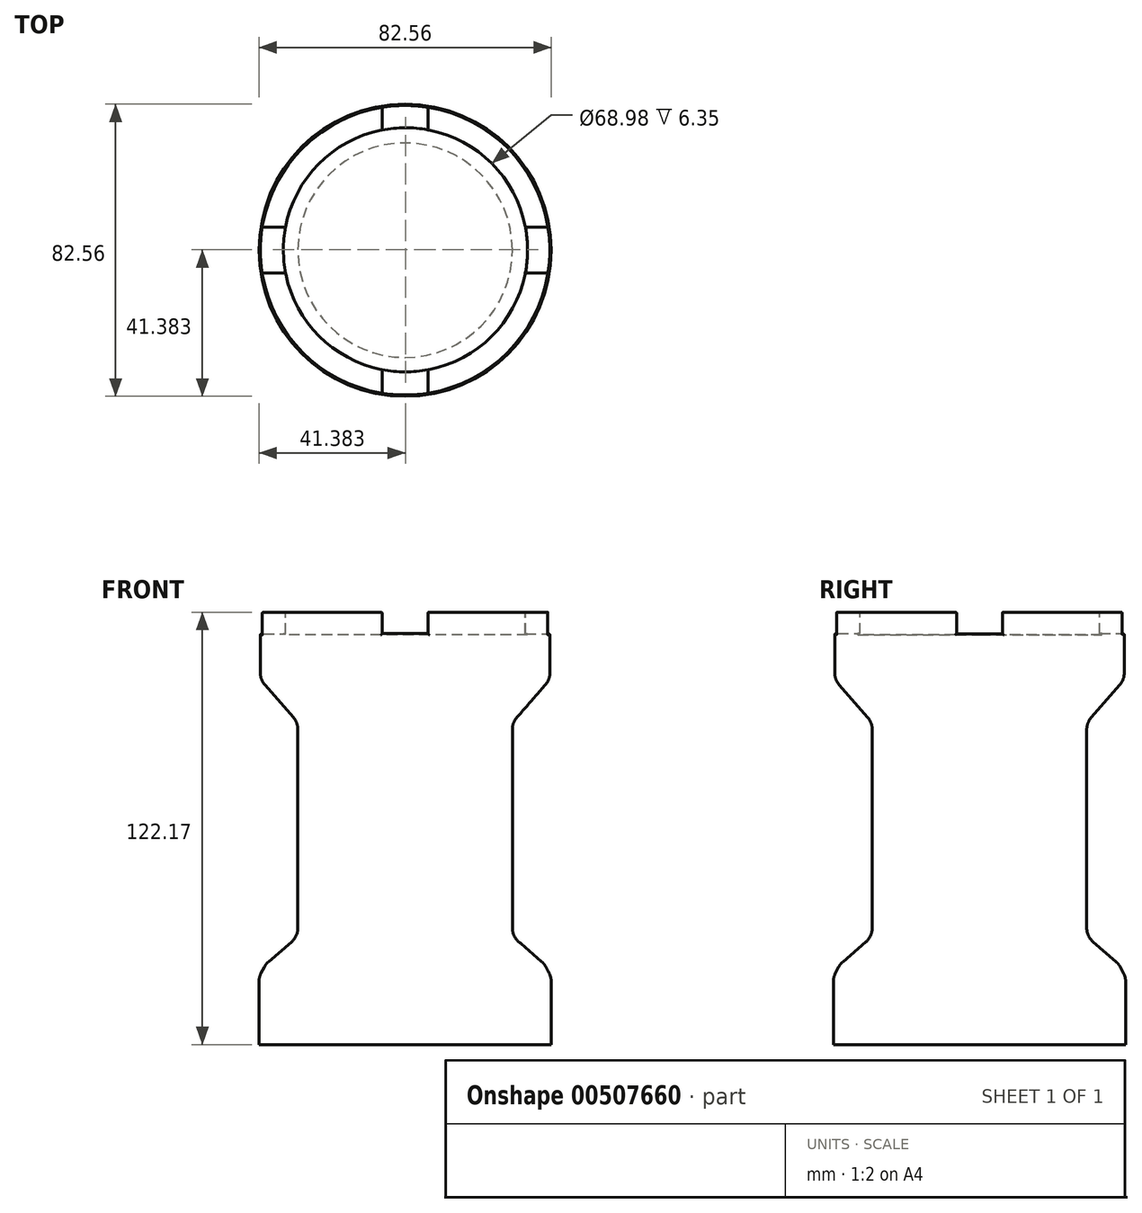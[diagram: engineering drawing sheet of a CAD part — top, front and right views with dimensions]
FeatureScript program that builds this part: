
annotation { "Feature Type Name" : "Feature", "Feature Type Description" : "" }
export const myFeature = defineFeature(function(context is Context, id is Id, definition is map)
    precondition{}
    {
        {
            var Q0;
            Q0=qCreatedBy(makeId("Top.planeOp"),FACE);
            var sketch = newSketch(context, id + "F0", { "sketchPlane" : qUnion([Q0])});
            skCircle(sketch, "E0", {"center": v(0, 0) * mm, "radius": 41.28 * mm});
            skSolve(sketch);
        }
        {
            var Q0;
            Q0=makeQuery(id+"F0.imprint","IMPRINT",FACE,{"disambiguationData":[TD([[makeQuery(id+"F0.imprint","IMPRINT",EDGE,{"derivedFrom":sQuery(id+"F0.wireOp",EDGE,"E0")}),1.0]])]});
            extrude(context, id + "F1", {"entities" : qUnion([Q0]), "depth" : 19.05 * mm, "offsetDistance" : 25.4 * mm});
        }
        {
            var Q0;
            Q0=makeQuery(id+"F1.opExtrude","CAP_FACE",FACE,{"disambiguationData":[OSD([sQuery(id+"F0.wireOp",EDGE,"E0")])],"isStart":false});
            extrude(context, id + "F2", {"entities" : qUnion([Q0]), "operationType" : NewBodyOperationType.ADD, "depth" : 3.68 * mm, "offsetDistance" : 25.4 * mm, "hasDraft" : true, "draftAngle" : 27.5 * degree, "draftPullDirection" : true});
        }
        {
            var Q0;
            Q0=makeQuery(id+"F2.opExtrude","CAP_FACE",FACE,{"disambiguationData":[OSD([sQuery(id+"F0.wireOp",EDGE,"E0")])],"isStart":false});
            extrude(context, id + "F3", {"entities" : qUnion([Q0]), "operationType" : NewBodyOperationType.ADD, "depth" : 7.87 * mm, "offsetDistance" : 25.4 * mm, "hasDraft" : true, "draftAngle" : 49 * degree, "draftPullDirection" : true});
        }
        {
            var Q0;
            Q0=makeQuery(id+"F3.opExtrude","CAP_FACE",FACE,{"disambiguationData":[OSD([sQuery(id+"F0.wireOp",EDGE,"E0")])],"isStart":false});
            extrude(context, id + "F4", {"entities" : qUnion([Q0]), "operationType" : NewBodyOperationType.ADD, "depth" : 60.32 * mm, "offsetDistance" : 25.4 * mm});
        }
        {
            var Q0;
            Q0=makeQuery(id+"F4.opExtrude","CAP_FACE",FACE,{"disambiguationData":[OSD([sQuery(id+"F0.wireOp",EDGE,"E0")])],"isStart":false});
            extrude(context, id + "F5", {"entities" : qUnion([Q0]), "operationType" : NewBodyOperationType.ADD, "depth" : 12.2 * mm, "offsetDistance" : 25.4 * mm, "hasDraft" : true, "draftAngle" : 41 * degree});
        }
        {
            var Q0;
            Q0=makeQuery(id+"F5.opExtrude","CAP_FACE",FACE,{"disambiguationData":[OSD([sQuery(id+"F0.wireOp",EDGE,"E0")])],"isStart":false});
            extrude(context, id + "F6", {"entities" : qUnion([Q0]), "operationType" : NewBodyOperationType.ADD, "depth" : 19.05 * mm, "offsetDistance" : 25.4 * mm});
        }
        {
            var Q0;
            Q0=makeQuery(id+"F6.opExtrude","CAP_FACE",FACE,{"disambiguationData":[OSD([sQuery(id+"F0.wireOp",EDGE,"E0")])],"isStart":false});
            var sketch = newSketch(context, id + "F7", { "sketchPlane" : qUnion([Q0])});
            skLineSegment(sketch, "E1", {"start": v(-40.9, 0) * mm, "end": v(-34.55, 0.09) * mm, "construction": true});
            skSolve(sketch);
        }
        {
            var Q0;
            Q0=makeQuery(id+"F7.imprint","IMPRINT",FACE,{"disambiguationData":[TD([[makeQuery(id+"F7.imprint","IMPRINT",EDGE,{"derivedFrom":makeQuery(id+"F6.opExtrude","CAP_EDGE",EDGE,{"disambiguationData":[OSD([sQuery(id+"F0.wireOp",EDGE,"E0")])],"isStart":false})}),1.0]])]});
            var sketch = newSketch(context, id + "F8", { "sketchPlane" : qUnion([Q0])});
            skCircle(sketch, "E2", {"center": v(0.1, 0.1) * mm, "radius": 34.5 * mm});
            skSolve(sketch);
        }
        {
            var Q0;
            Q0=makeQuery(id+"F8.imprint","IMPRINT",FACE,{"disambiguationData":[TD([[makeQuery(id+"F8.imprint","IMPRINT",EDGE,{"derivedFrom":sQuery(id+"F8.wireOp",EDGE,"E2")}),1.0]])]});
            var Q1;
            Q1=sQuery(id+"F8.wireOp",EDGE,"E2");
            extrude(context, id + "F9", {"entities" : qUnion([Q0]), "operationType" : NewBodyOperationType.REMOVE, "surfaceEntities" : qUnion([Q1]), "oppositeDirection" : true, "depth" : 6.35 * mm, "offsetDistance" : 25.4 * mm});
        }
        {
            var Q0;
            Q0=qCreatedBy(makeId("Front.planeOp"),FACE);
            var sketch = newSketch(context, id + "F10", { "sketchPlane" : qUnion([Q0])});
            skLineSegment(sketch, "E3.bottom", {"start": v(6.45, 116.1) * mm, "end": v(-6.45, 116.1) * mm});
            skLineSegment(sketch, "E3.top", {"start": v(6.45, 128.67) * mm, "end": v(-6.45, 128.67) * mm});
            skLineSegment(sketch, "E3.left", {"start": v(6.45, 116.1) * mm, "end": v(6.45, 128.67) * mm});
            skLineSegment(sketch, "E3.right", {"start": v(-6.45, 116.1) * mm, "end": v(-6.45, 128.67) * mm});
            skPoint(sketch, "E3.middle", {"position": v(0, 122.38) * mm});
            skSolve(sketch);
        }
        {
            var Q0;
            Q0=makeQuery(id+"F10.imprint","IMPRINT",FACE,{"disambiguationData":[TD([[makeQuery(id+"F10.imprint","IMPRINT",EDGE,{"derivedFrom":sQuery(id+"F10.wireOp",EDGE,"E3.bottom")}),-1.0]])]});
            extrude(context, id + "F11", {"entities" : qUnion([Q0]), "operationType" : NewBodyOperationType.REMOVE, "endBound" : BoundingType.SYMMETRIC, "depth" : 108.7 * mm, "offsetDistance" : 25.4 * mm});
        }
        {
            var Q0;
            Q0=qCreatedBy(makeId("Right.planeOp"),FACE);
            var sketch = newSketch(context, id + "F12", { "sketchPlane" : qUnion([Q0])});
            skLineSegment(sketch, "E4.bottom", {"start": v(-6.5, 116.05) * mm, "end": v(6.5, 116.05) * mm});
            skLineSegment(sketch, "E4.top", {"start": v(-6.5, 129.22) * mm, "end": v(6.5, 129.22) * mm});
            skLineSegment(sketch, "E4.left", {"start": v(-6.5, 116.05) * mm, "end": v(-6.5, 129.22) * mm});
            skLineSegment(sketch, "E4.right", {"start": v(6.5, 116.05) * mm, "end": v(6.5, 129.22) * mm});
            skPoint(sketch, "E4.middle", {"position": v(0, 122.64) * mm});
            skSolve(sketch);
        }
        {
            var Q0;
            Q0=makeQuery(id+"F12.imprint","IMPRINT",FACE,{"disambiguationData":[TD([[makeQuery(id+"F12.imprint","IMPRINT",EDGE,{"derivedFrom":sQuery(id+"F12.wireOp",EDGE,"E4.bottom")}),1.0]])]});
            extrude(context, id + "F13", {"entities" : qUnion([Q0]), "operationType" : NewBodyOperationType.REMOVE, "endBound" : BoundingType.SYMMETRIC, "oppositeDirection" : true, "depth" : 115.32 * mm, "offsetDistance" : 25.4 * mm});
        }
        {
            var Q0;
            {var subQ0=sQuery(id+"F0.wireOp",EDGE,"E0");Q0=makeQuery(id+"F6.boolean.opBoolean","MERGE",EDGE,{"derivedFrom":[makeQuery(id+"F5.opExtrude","CAP_EDGE",EDGE,{"disambiguationData":[OSD([subQ0])],"isStart":false}),makeQuery(id+"F6.opExtrude","CAP_EDGE",EDGE,{"disambiguationData":[OSD([subQ0])],"isStart":true})]});}
            var Q1;
            {var subQ0=sQuery(id+"F0.wireOp",EDGE,"E0");Q1=makeQuery(id+"F5.boolean.opBoolean","MERGE",EDGE,{"derivedFrom":[makeQuery(id+"F4.opExtrude","CAP_EDGE",EDGE,{"disambiguationData":[OSD([subQ0])],"isStart":false}),makeQuery(id+"F5.opExtrude","CAP_EDGE",EDGE,{"disambiguationData":[OSD([subQ0])],"isStart":true})]});}
            fillet(context, id + "F14", {"entities" : qUnion([Q0, Q1]), "radius" : 5.08 * mm, "tangentPropagation" : true, "allowEdgeOverflow" : false});
        }
        {
            var Q0;
            {var subQ0=sQuery(id+"F0.wireOp",EDGE,"E0");Q0=makeQuery(id+"F4.boolean.opBoolean","MERGE",EDGE,{"derivedFrom":[makeQuery(id+"F3.opExtrude","CAP_EDGE",EDGE,{"disambiguationData":[OSD([subQ0])],"isStart":false}),makeQuery(id+"F4.opExtrude","CAP_EDGE",EDGE,{"disambiguationData":[OSD([subQ0])],"isStart":true})]});}
            var Q1;
            {var subQ0=sQuery(id+"F0.wireOp",EDGE,"E0");Q1=makeQuery(id+"F3.boolean.opBoolean","MERGE",EDGE,{"derivedFrom":[makeQuery(id+"F2.opExtrude","CAP_EDGE",EDGE,{"disambiguationData":[OSD([subQ0])],"isStart":false}),makeQuery(id+"F3.opExtrude","CAP_EDGE",EDGE,{"disambiguationData":[OSD([subQ0])],"isStart":true})]});}
            fillet(context, id + "F15", {"entities" : qUnion([Q0, Q1]), "radius" : 5.08 * mm, "tangentPropagation" : true, "allowEdgeOverflow" : false});
        }
        {
            var Q0;
            {var subQ0=sQuery(id+"F0.wireOp",EDGE,"E0");Q0=makeQuery(id+"F2.boolean.opBoolean","MERGE",EDGE,{"derivedFrom":[makeQuery(id+"F1.opExtrude","CAP_EDGE",EDGE,{"disambiguationData":[OSD([subQ0])],"isStart":false}),makeQuery(id+"F2.opExtrude","CAP_EDGE",EDGE,{"disambiguationData":[OSD([subQ0])],"isStart":true})]});}
            fillet(context, id + "F16", {"entities" : qUnion([Q0]), "radius" : 5.08 * mm, "tangentPropagation" : true, "allowEdgeOverflow" : false});
        }
        {
            var Q0;
            {var subQ1=sQuery(id+"F8.wireOp",EDGE,"E2");var subQ3=makeQuery(id+"F11.opExtrude","SWEPT_FACE",FACE,{"disambiguationData":[OSD([sQuery(id+"F10.wireOp",EDGE,"E3.left")])]});Q0=makeQuery(id+"F13.boolean.opBoolean","SPLIT",EDGE,{"disambiguationData":[TD([makeQuery(id+"F11.boolean.opBoolean","COPY",FACE,{"disambiguationData":[OD(0.0)],"derivedFrom":subQ3})])],"derivedFrom":makeQuery(id+"F11.boolean.opBoolean","SPLIT",EDGE,{"disambiguationData":[TD([subQ3])],"derivedFrom":makeQuery(id+"F9.boolean.opBoolean","COPY",EDGE,{"derivedFrom":makeQuery(id+"F9.opExtrude","CAP_EDGE",EDGE,{"disambiguationData":[OSD([subQ1])],"isStart":true})})})});}
            var Q1;
            {var subQ1=sQuery(id+"F8.wireOp",EDGE,"E2");var subQ3=makeQuery(id+"F11.opExtrude","SWEPT_FACE",FACE,{"disambiguationData":[OSD([sQuery(id+"F10.wireOp",EDGE,"E3.right")])]});Q1=makeQuery(id+"F13.boolean.opBoolean","SPLIT",EDGE,{"disambiguationData":[TD([makeQuery(id+"F11.boolean.opBoolean","COPY",FACE,{"disambiguationData":[OD(0.0)],"derivedFrom":subQ3})])],"derivedFrom":makeQuery(id+"F11.boolean.opBoolean","SPLIT",EDGE,{"disambiguationData":[TD([subQ3])],"derivedFrom":makeQuery(id+"F9.boolean.opBoolean","COPY",EDGE,{"derivedFrom":makeQuery(id+"F9.opExtrude","CAP_EDGE",EDGE,{"disambiguationData":[OSD([subQ1])],"isStart":true})})})});}
            var Q2;
            {var subQ1=sQuery(id+"F8.wireOp",EDGE,"E2");var subQ3=makeQuery(id+"F11.opExtrude","SWEPT_FACE",FACE,{"disambiguationData":[OSD([sQuery(id+"F10.wireOp",EDGE,"E3.right")])]});Q2=makeQuery(id+"F13.boolean.opBoolean","SPLIT",EDGE,{"disambiguationData":[TD([makeQuery(id+"F11.boolean.opBoolean","COPY",FACE,{"disambiguationData":[OD(1.0)],"derivedFrom":subQ3})])],"derivedFrom":makeQuery(id+"F11.boolean.opBoolean","SPLIT",EDGE,{"disambiguationData":[TD([subQ3])],"derivedFrom":makeQuery(id+"F9.boolean.opBoolean","COPY",EDGE,{"derivedFrom":makeQuery(id+"F9.opExtrude","CAP_EDGE",EDGE,{"disambiguationData":[OSD([subQ1])],"isStart":true})})})});}
            var Q3;
            {var subQ1=sQuery(id+"F8.wireOp",EDGE,"E2");var subQ3=makeQuery(id+"F11.opExtrude","SWEPT_FACE",FACE,{"disambiguationData":[OSD([sQuery(id+"F10.wireOp",EDGE,"E3.left")])]});Q3=makeQuery(id+"F13.boolean.opBoolean","SPLIT",EDGE,{"disambiguationData":[TD([makeQuery(id+"F11.boolean.opBoolean","COPY",FACE,{"disambiguationData":[OD(1.0)],"derivedFrom":subQ3})])],"derivedFrom":makeQuery(id+"F11.boolean.opBoolean","SPLIT",EDGE,{"disambiguationData":[TD([subQ3])],"derivedFrom":makeQuery(id+"F9.boolean.opBoolean","COPY",EDGE,{"derivedFrom":makeQuery(id+"F9.opExtrude","CAP_EDGE",EDGE,{"disambiguationData":[OSD([subQ1])],"isStart":true})})})});}
            var Q4;
            {var subQ0=sQuery(id+"F0.wireOp",EDGE,"E0");Q4=makeQuery(id+"F13.boolean.opBoolean","INTERSECT",EDGE,{"derivedFrom":[makeQuery(id+"F11.boolean.opBoolean","SPLIT",FACE,{"disambiguationData":[TD([makeQuery(id+"F11.opExtrude","SWEPT_FACE",FACE,{"disambiguationData":[OSD([sQuery(id+"F10.wireOp",EDGE,"E3.left")])]})])],"derivedFrom":makeQuery(id+"F6.opExtrude","CAP_FACE",FACE,{"disambiguationData":[OSD([subQ0])],"isStart":false})}),makeQuery(id+"F13.opExtrude","SWEPT_FACE",FACE,{"disambiguationData":[OSD([sQuery(id+"F12.wireOp",EDGE,"E4.left")])]})]});}
            var Q5;
            {var subQ0=sQuery(id+"F0.wireOp",EDGE,"E0");Q5=makeQuery(id+"F13.boolean.opBoolean","INTERSECT",EDGE,{"derivedFrom":[makeQuery(id+"F11.boolean.opBoolean","SPLIT",FACE,{"disambiguationData":[TD([makeQuery(id+"F11.opExtrude","SWEPT_FACE",FACE,{"disambiguationData":[OSD([sQuery(id+"F10.wireOp",EDGE,"E3.left")])]})])],"derivedFrom":makeQuery(id+"F6.opExtrude","CAP_FACE",FACE,{"disambiguationData":[OSD([subQ0])],"isStart":false})}),makeQuery(id+"F13.opExtrude","SWEPT_FACE",FACE,{"disambiguationData":[OSD([sQuery(id+"F12.wireOp",EDGE,"E4.right")])]})]});}
            var Q6;
            Q6=makeQuery(id+"F11.boolean.opBoolean","INTERSECT",EDGE,{"disambiguationData":[OD(0.0)],"derivedFrom":[makeQuery(id+"F6.opExtrude","CAP_FACE",FACE,{"disambiguationData":[OSD([sQuery(id+"F0.wireOp",EDGE,"E0")])],"isStart":false}),makeQuery(id+"F11.opExtrude","SWEPT_FACE",FACE,{"disambiguationData":[OSD([sQuery(id+"F10.wireOp",EDGE,"E3.left")])]})]});
            var Q7;
            Q7=makeQuery(id+"F11.boolean.opBoolean","INTERSECT",EDGE,{"disambiguationData":[OD(0.0)],"derivedFrom":[makeQuery(id+"F6.opExtrude","CAP_FACE",FACE,{"disambiguationData":[OSD([sQuery(id+"F0.wireOp",EDGE,"E0")])],"isStart":false}),makeQuery(id+"F11.opExtrude","SWEPT_FACE",FACE,{"disambiguationData":[OSD([sQuery(id+"F10.wireOp",EDGE,"E3.right")])]})]});
            var Q8;
            {var subQ0=sQuery(id+"F0.wireOp",EDGE,"E0");var subQ2=makeQuery(id+"F11.opExtrude","SWEPT_FACE",FACE,{"disambiguationData":[OSD([sQuery(id+"F10.wireOp",EDGE,"E3.left")])]});Q8=makeQuery(id+"F13.boolean.opBoolean","SPLIT",EDGE,{"disambiguationData":[TD([makeQuery(id+"F11.boolean.opBoolean","COPY",FACE,{"disambiguationData":[OD(1.0)],"derivedFrom":subQ2})])],"derivedFrom":makeQuery(id+"F11.boolean.opBoolean","SPLIT",EDGE,{"disambiguationData":[TD([subQ2])],"derivedFrom":makeQuery(id+"F6.opExtrude","CAP_EDGE",EDGE,{"disambiguationData":[OSD([subQ0])],"isStart":false})})});}
            var Q9;
            Q9=makeQuery(id+"F11.boolean.opBoolean","INTERSECT",EDGE,{"disambiguationData":[OD(1.0)],"derivedFrom":[makeQuery(id+"F6.opExtrude","CAP_FACE",FACE,{"disambiguationData":[OSD([sQuery(id+"F0.wireOp",EDGE,"E0")])],"isStart":false}),makeQuery(id+"F11.opExtrude","SWEPT_FACE",FACE,{"disambiguationData":[OSD([sQuery(id+"F10.wireOp",EDGE,"E3.right")])]})]});
            var Q10;
            Q10=makeQuery(id+"F11.boolean.opBoolean","INTERSECT",EDGE,{"disambiguationData":[OD(1.0)],"derivedFrom":[makeQuery(id+"F6.opExtrude","CAP_FACE",FACE,{"disambiguationData":[OSD([sQuery(id+"F0.wireOp",EDGE,"E0")])],"isStart":false}),makeQuery(id+"F11.opExtrude","SWEPT_FACE",FACE,{"disambiguationData":[OSD([sQuery(id+"F10.wireOp",EDGE,"E3.left")])]})]});
            var Q11;
            {var subQ0=sQuery(id+"F0.wireOp",EDGE,"E0");var subQ3=makeQuery(id+"F11.opExtrude","SWEPT_FACE",FACE,{"disambiguationData":[OSD([sQuery(id+"F10.wireOp",EDGE,"E3.right")])]});Q11=makeQuery(id+"F13.boolean.opBoolean","SPLIT",EDGE,{"disambiguationData":[TD([makeQuery(id+"F11.boolean.opBoolean","COPY",FACE,{"disambiguationData":[OD(1.0)],"derivedFrom":subQ3})])],"derivedFrom":makeQuery(id+"F11.boolean.opBoolean","SPLIT",EDGE,{"disambiguationData":[TD([subQ3])],"derivedFrom":makeQuery(id+"F6.opExtrude","CAP_EDGE",EDGE,{"disambiguationData":[OSD([subQ0])],"isStart":false})})});}
            var Q12;
            {var subQ0=sQuery(id+"F0.wireOp",EDGE,"E0");Q12=makeQuery(id+"F13.boolean.opBoolean","INTERSECT",EDGE,{"derivedFrom":[makeQuery(id+"F11.boolean.opBoolean","SPLIT",FACE,{"disambiguationData":[TD([makeQuery(id+"F11.opExtrude","SWEPT_FACE",FACE,{"disambiguationData":[OSD([sQuery(id+"F10.wireOp",EDGE,"E3.right")])]})])],"derivedFrom":makeQuery(id+"F6.opExtrude","CAP_FACE",FACE,{"disambiguationData":[OSD([subQ0])],"isStart":false})}),makeQuery(id+"F13.opExtrude","SWEPT_FACE",FACE,{"disambiguationData":[OSD([sQuery(id+"F12.wireOp",EDGE,"E4.left")])]})]});}
            var Q13;
            {var subQ0=sQuery(id+"F0.wireOp",EDGE,"E0");var subQ3=makeQuery(id+"F11.opExtrude","SWEPT_FACE",FACE,{"disambiguationData":[OSD([sQuery(id+"F10.wireOp",EDGE,"E3.right")])]});Q13=makeQuery(id+"F13.boolean.opBoolean","SPLIT",EDGE,{"disambiguationData":[TD([makeQuery(id+"F11.boolean.opBoolean","COPY",FACE,{"disambiguationData":[OD(0.0)],"derivedFrom":subQ3})])],"derivedFrom":makeQuery(id+"F11.boolean.opBoolean","SPLIT",EDGE,{"disambiguationData":[TD([subQ3])],"derivedFrom":makeQuery(id+"F6.opExtrude","CAP_EDGE",EDGE,{"disambiguationData":[OSD([subQ0])],"isStart":false})})});}
            var Q14;
            Q14=makeQuery(id+"F13.boolean.opBoolean","INTERSECT",EDGE,{"disambiguationData":[OD(0.0)],"derivedFrom":[makeQuery(id+"F6.opExtrude","SWEPT_FACE",FACE,{"disambiguationData":[OSD([sQuery(id+"F0.wireOp",EDGE,"E0")])]}),makeQuery(id+"F13.opExtrude","SWEPT_FACE",FACE,{"disambiguationData":[OSD([sQuery(id+"F12.wireOp",EDGE,"E4.left")])]})]});
            var Q15;
            Q15=makeQuery(id+"F13.boolean.opBoolean","INTERSECT",EDGE,{"disambiguationData":[OD(0.0)],"derivedFrom":[makeQuery(id+"F6.opExtrude","SWEPT_FACE",FACE,{"disambiguationData":[OSD([sQuery(id+"F0.wireOp",EDGE,"E0")])]}),makeQuery(id+"F13.opExtrude","SWEPT_FACE",FACE,{"disambiguationData":[OSD([sQuery(id+"F12.wireOp",EDGE,"E4.bottom")])]})]});
            var Q16;
            Q16=makeQuery(id+"F13.boolean.opBoolean","INTERSECT",EDGE,{"disambiguationData":[OD(0.0)],"derivedFrom":[makeQuery(id+"F6.opExtrude","SWEPT_FACE",FACE,{"disambiguationData":[OSD([sQuery(id+"F0.wireOp",EDGE,"E0")])]}),makeQuery(id+"F13.opExtrude","SWEPT_FACE",FACE,{"disambiguationData":[OSD([sQuery(id+"F12.wireOp",EDGE,"E4.right")])]})]});
            var Q17;
            Q17=makeQuery(id+"F11.boolean.opBoolean","INTERSECT",EDGE,{"disambiguationData":[OD(0.0)],"derivedFrom":[makeQuery(id+"F6.opExtrude","SWEPT_FACE",FACE,{"disambiguationData":[OSD([sQuery(id+"F0.wireOp",EDGE,"E0")])]}),makeQuery(id+"F11.opExtrude","SWEPT_FACE",FACE,{"disambiguationData":[OSD([sQuery(id+"F10.wireOp",EDGE,"E3.right")])]})]});
            var Q18;
            Q18=makeQuery(id+"F11.boolean.opBoolean","INTERSECT",EDGE,{"disambiguationData":[OD(0.0)],"derivedFrom":[makeQuery(id+"F6.opExtrude","SWEPT_FACE",FACE,{"disambiguationData":[OSD([sQuery(id+"F0.wireOp",EDGE,"E0")])]}),makeQuery(id+"F11.opExtrude","SWEPT_FACE",FACE,{"disambiguationData":[OSD([sQuery(id+"F10.wireOp",EDGE,"E3.bottom")])]})]});
            var Q19;
            Q19=makeQuery(id+"F11.boolean.opBoolean","INTERSECT",EDGE,{"disambiguationData":[OD(0.0)],"derivedFrom":[makeQuery(id+"F6.opExtrude","SWEPT_FACE",FACE,{"disambiguationData":[OSD([sQuery(id+"F0.wireOp",EDGE,"E0")])]}),makeQuery(id+"F11.opExtrude","SWEPT_FACE",FACE,{"disambiguationData":[OSD([sQuery(id+"F10.wireOp",EDGE,"E3.left")])]})]});
            var Q20;
            Q20=makeQuery(id+"F13.boolean.opBoolean","INTERSECT",EDGE,{"disambiguationData":[OD(1.0)],"derivedFrom":[makeQuery(id+"F6.opExtrude","SWEPT_FACE",FACE,{"disambiguationData":[OSD([sQuery(id+"F0.wireOp",EDGE,"E0")])]}),makeQuery(id+"F13.opExtrude","SWEPT_FACE",FACE,{"disambiguationData":[OSD([sQuery(id+"F12.wireOp",EDGE,"E4.left")])]})]});
            var Q21;
            Q21=makeQuery(id+"F13.boolean.opBoolean","INTERSECT",EDGE,{"disambiguationData":[OD(1.0)],"derivedFrom":[makeQuery(id+"F6.opExtrude","SWEPT_FACE",FACE,{"disambiguationData":[OSD([sQuery(id+"F0.wireOp",EDGE,"E0")])]}),makeQuery(id+"F13.opExtrude","SWEPT_FACE",FACE,{"disambiguationData":[OSD([sQuery(id+"F12.wireOp",EDGE,"E4.bottom")])]})]});
            var Q22;
            Q22=makeQuery(id+"F13.boolean.opBoolean","INTERSECT",EDGE,{"disambiguationData":[OD(1.0)],"derivedFrom":[makeQuery(id+"F6.opExtrude","SWEPT_FACE",FACE,{"disambiguationData":[OSD([sQuery(id+"F0.wireOp",EDGE,"E0")])]}),makeQuery(id+"F13.opExtrude","SWEPT_FACE",FACE,{"disambiguationData":[OSD([sQuery(id+"F12.wireOp",EDGE,"E4.right")])]})]});
            var Q23;
            Q23=makeQuery(id+"F11.boolean.opBoolean","INTERSECT",EDGE,{"disambiguationData":[OD(1.0)],"derivedFrom":[makeQuery(id+"F6.opExtrude","SWEPT_FACE",FACE,{"disambiguationData":[OSD([sQuery(id+"F0.wireOp",EDGE,"E0")])]}),makeQuery(id+"F11.opExtrude","SWEPT_FACE",FACE,{"disambiguationData":[OSD([sQuery(id+"F10.wireOp",EDGE,"E3.right")])]})]});
            var Q24;
            Q24=makeQuery(id+"F11.boolean.opBoolean","INTERSECT",EDGE,{"disambiguationData":[OD(1.0)],"derivedFrom":[makeQuery(id+"F6.opExtrude","SWEPT_FACE",FACE,{"disambiguationData":[OSD([sQuery(id+"F0.wireOp",EDGE,"E0")])]}),makeQuery(id+"F11.opExtrude","SWEPT_FACE",FACE,{"disambiguationData":[OSD([sQuery(id+"F10.wireOp",EDGE,"E3.left")])]})]});
            var Q25;
            Q25=makeQuery(id+"F11.boolean.opBoolean","INTERSECT",EDGE,{"disambiguationData":[OD(1.0)],"derivedFrom":[makeQuery(id+"F6.opExtrude","SWEPT_FACE",FACE,{"disambiguationData":[OSD([sQuery(id+"F0.wireOp",EDGE,"E0")])]}),makeQuery(id+"F11.opExtrude","SWEPT_FACE",FACE,{"disambiguationData":[OSD([sQuery(id+"F10.wireOp",EDGE,"E3.bottom")])]})]});
            fillet(context, id + "F17", {"entities" : qUnion([Q0, Q1, Q2, Q3, Q4, Q5, Q6, Q7, Q8, Q9, Q10, Q11, Q12, Q13, Q14, Q15, Q16, Q17, Q18, Q19, Q20, Q21, Q22, Q23, Q24, Q25]), "radius" : 0.32 * mm, "tangentPropagation" : true, "allowEdgeOverflow" : false});
        }
    });
